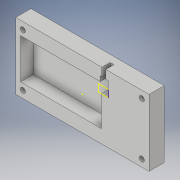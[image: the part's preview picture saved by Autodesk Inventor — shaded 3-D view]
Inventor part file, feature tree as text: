
AUTODESK INVENTOR PART (.ipt)
format: ipt  version: 2018 (Build 220112000, 112)  size: 279,040 bytes
history: native  units: in
note: dims shown in document units (in); Inventor stores cm internally (conversion verified against a paired STEP export)
features: extrude x11, sketch x8, projected_geometry x5, plane x4, hole x2
ambient origin geometry x8: Origin, YZ Plane, XZ Plane, XY Plane, X Axis, Y Axis, Z Axis, Center Point
bodies: Solid1 (feature_tree)
feature tree (30):
  extrude  "Extrusion1"  Depth=3.5in
  extrude  "Extrusion2"  Depth=2.105in
  extrude  "Extrusion4"  Depth=0.25in
  plane  "Work Plane1"
  plane  "Work Plane2"
  extrude  "Extrusion5"  Depth=0.38in
  plane  "Work Plane3"
  plane  "Work Plane4"
  sketch  "Sketch6"  dims[d4=0.25in d5=4.075in]
  extrude  "Extrusion6"  Depth=0.675in
  extrude  "Extrusion7"  Depth=0.2in
  extrude  "Extrusion8"  Depth=0.125in TaperAngle=0.0deg
  extrude  "Extrusion9"  Depth=0.25in
  extrude  "Extrusion10"  Depth=0.25in
  hole  "Hole2"  [1 undecoded]
  extrude  "Extrusion11"  Depth=0.25in
  extrude  "Extrusion12"  Depth=0.25in
  sketch  "Sketch3"  dims[d0=7.0in d1=3.5in]
  projected_geometry  "Projected Loop2"
  sketch  "Sketch5"  dims[d2=4.25in d3=2.105in]
  projected_geometry  "Projected Loop3"
  sketch  "Sketch7"  dims[d7=0.33in d8=0.38in]
  projected_geometry  "Projected Loop4"
  sketch  "Sketch8"  dims[d9=0.675in d10=0.0in d13=0.525in]
  sketch  "Sketch9"  dims[d15=0.2in d17=0.4in]
  hole  "Hole1"  [1 undecoded]
  sketch  "Sketch10"  dims[d18=0.5in d19=0.0in d22=0.125in d23=0.0in]
  projected_geometry  "Projected Loop5"
  sketch  "Sketch12"  dims[d24=0.0625in d25=0.22in d26=1.45in d27=2.0in d28=0.75in d29=0.25in d30=0.125in d31=0.0in d32=0.5in d33=0.125in d34=0.125in d35=0.875in d36=0.375in d37=0.0in d38=0.375in d39=0.0in d40=0.25in d41=0.0in d42=0.25in d43=0.0in d44=0.25in d45=0.0in d46=0.266in d47=0.75in d48=0.375in d49=0.25in d50=0.5635in d51=1.0in d52=0.0in d53=0.25in d54=0.0in d55=1.0in d56=0.0in]
  projected_geometry  "Projected Loop13"
note: 2 required parameter values undecoded (feature->parameter linkage not recoverable at this tier; creation-order binding heuristic only, values carry confidence <= 0.55)
